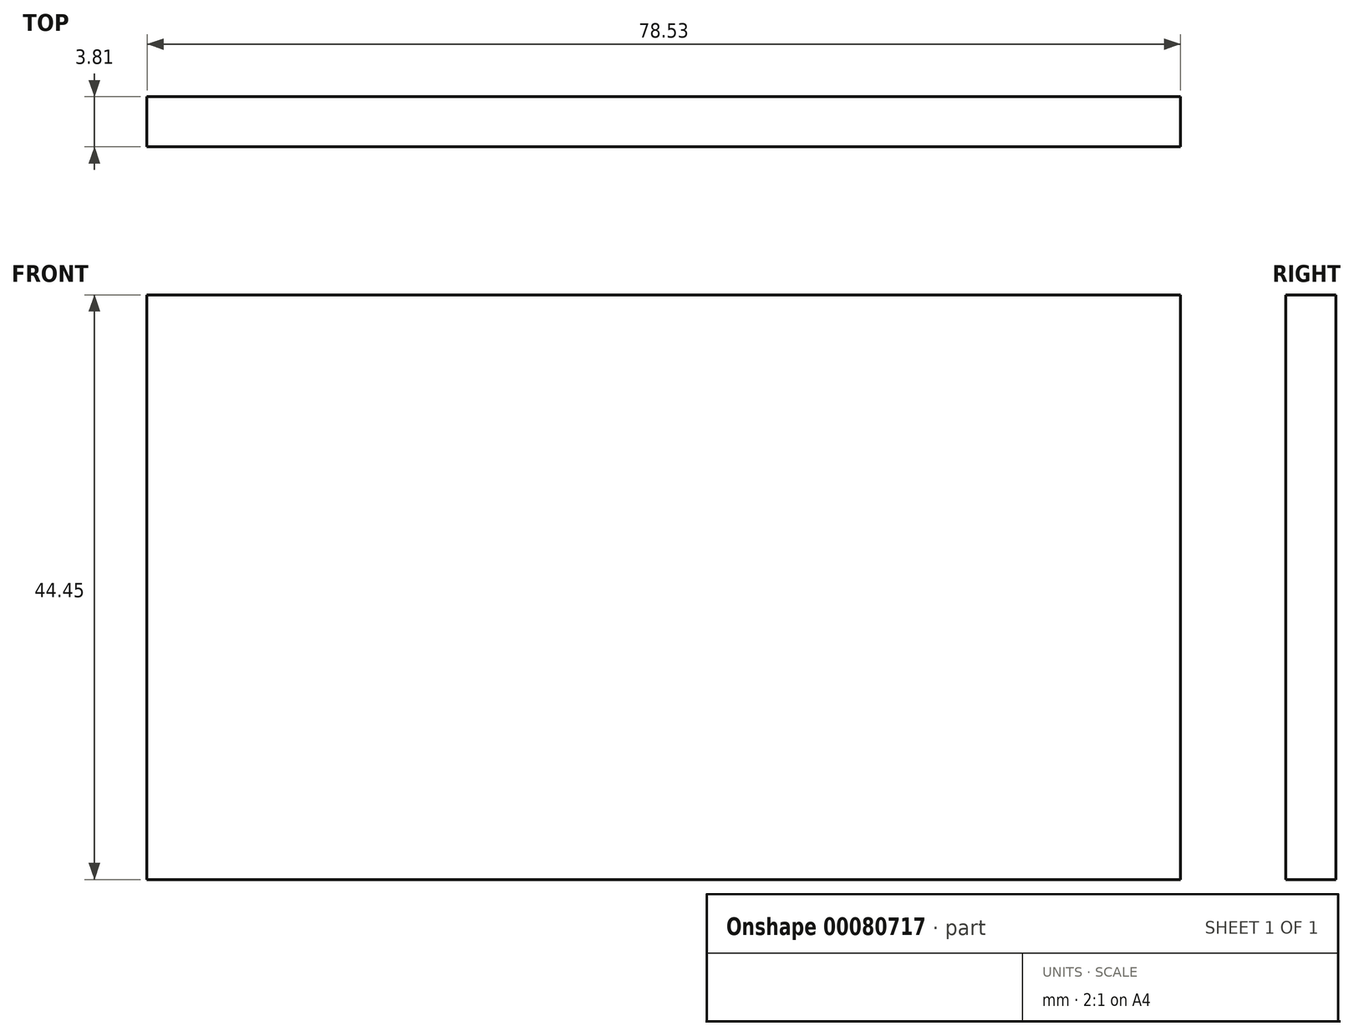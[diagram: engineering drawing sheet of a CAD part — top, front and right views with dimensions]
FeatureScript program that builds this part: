
annotation { "Feature Type Name" : "Feature", "Feature Type Description" : "" }
export const myFeature = defineFeature(function(context is Context, id is Id, definition is map)
    precondition{}
    {
        {
            var Q0;
            Q0=qCreatedBy(makeId("Front.planeOp"),FACE);
            var sketch = newSketch(context, id + "F0", { "sketchPlane" : qUnion([Q0])});
            skLineSegment(sketch, "E0.bottom", {"start": v(-38.5, 33.65) * mm, "end": v(40.04, 33.65) * mm});
            skLineSegment(sketch, "E0.top", {"start": v(-38.5, -10.8) * mm, "end": v(40.04, -10.8) * mm});
            skLineSegment(sketch, "E0.left", {"start": v(-38.5, 33.65) * mm, "end": v(-38.5, -10.8) * mm});
            skLineSegment(sketch, "E0.right", {"start": v(40.04, 33.65) * mm, "end": v(40.04, -10.8) * mm});
            skSolve(sketch);
        }
        {
            var Q0;
            Q0=makeQuery(id+"F0.imprint","IMPRINT",FACE,{"disambiguationData":[TD([[makeQuery(id+"F0.imprint","IMPRINT",EDGE,{"derivedFrom":sQuery(id+"F0.wireOp",EDGE,"E0.bottom")}),-1.0]])]});
            extrude(context, id + "F1", {"entities" : qUnion([Q0]), "depth" : 3.8 * mm});
        }
    });
